# Revit family: Термостатический клапан для 2трубных систем проходной
name_source: partatom
category: Арматура трубопроводов
revit_build: Autodesk Revit 2017 (Build: 20171027_0315(x64)
units: mm (PartAtom-declared; Revit-internal decimal feet)

## family parameters
Всегда вертикально = Да
На основе рабочей плоскости = Нет
Общий = Нет
При загрузке вырезать с полостями = Нет
Размер круглого соединителя = Использовать радиус
Тип детали = Вставляется

## types (2) — shared parameters
ADSK_Единица измерения = шт
ADSK_Завод-изготовитель = Meibes
ADSK_Наименование = Клапан термостатический для двухтрубных систем проходной
H = 22 мм
URL = http://www.meibes.ru
t = 3 мм
Группа модели = Клапан термостатический для двухтрубных систем проходной
Изготовитель = Meibes
Материал полимера = Фильтр_Черный
Материал стальной части = Фильтр_Латунь
Материал фитинга = РВК_Полипропилен PPR
Разработчик = ООО ПРОРУБИМ
Разработчик (телефон) = +7(495)649-85-43
Разработчик модели (URL) = http://prorubim.com
zero-valued in all types: ADSK_Масса

## per-type parameters (varying)
| type | ADSK_Код изделия | DN | R | l1 | l2 | l3 |
| DN15 | RW 123 804 1 | 15 мм | 8 мм | 95 мм | 66 мм | 29 мм |
| DN20 | RW 123 805 1 | 20 мм | 10 мм | 105 мм | 74 мм | 34 мм |

note: column(s) folded — value = type name in every type: ADSK_Обозначение
